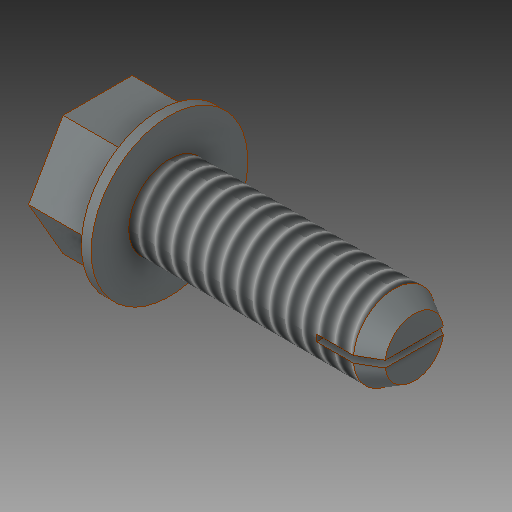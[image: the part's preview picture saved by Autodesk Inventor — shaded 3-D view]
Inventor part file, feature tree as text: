
AUTODESK INVENTOR PART (.ipt)
format: ipt  version: 2018 (Build 220112000, 112)  size: 183,808 bytes
history: native  units: in
note: dims shown in document units (in); Inventor stores cm internally (conversion verified against a paired STEP export)
features: thread x1, other x1
ambient origin geometry x8: Origin, YZ Plane, XZ Plane, XY Plane, X Axis, Y Axis, Z Axis, Center Point
bodies: Solid1 (feature_tree)
feature tree (2):
  thread  "Thread1"  [1 undecoded]
  other  "point_Cut-Extrude10"
note: 1 required parameter value undecoded (feature->parameter linkage not recoverable at this tier; creation-order binding heuristic only, values carry confidence <= 0.55)
